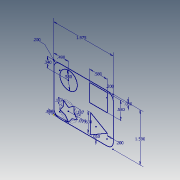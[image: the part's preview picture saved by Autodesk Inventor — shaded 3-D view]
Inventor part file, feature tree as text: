
AUTODESK INVENTOR PART (.ipt)
format: ipt  version: 2015 (Build 190159000, 159)  size: 87,040 bytes
history: native  units: in
note: dims shown in document units (in); Inventor stores cm internally (conversion verified against a paired STEP export)
features: sketch x1
ambient origin geometry x8: Origin, YZ Plane, XZ Plane, XY Plane, X Axis, Y Axis, Z Axis, Center Point
feature tree (1):
  sketch  "Sketch1"  dims[d0=1.975in d1=1.59in d2=0.2in d3=0.58in d4=0.49in d5=0.34in d6=0.58in d7=0.58in d8=0.05in d9=0.2in d20=0.638in d21=0.05in d22=0.2in d23=0.187in d24=0.187in d25=0.0935in d26=0.488in d27=0.05in]
